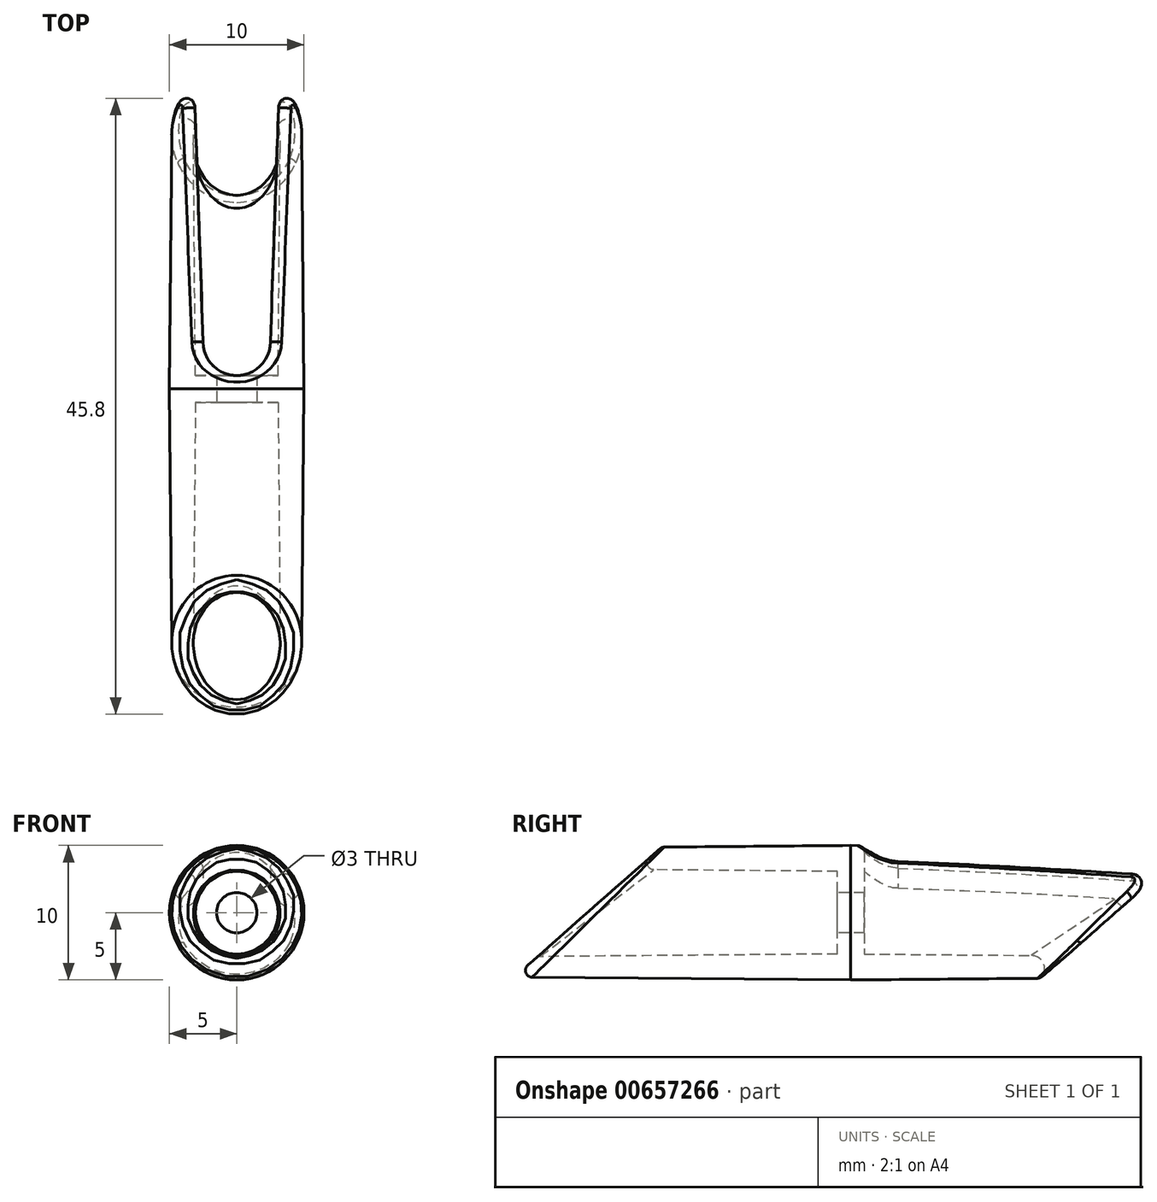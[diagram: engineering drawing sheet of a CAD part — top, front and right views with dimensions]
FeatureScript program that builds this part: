
annotation { "Feature Type Name" : "Feature", "Feature Type Description" : "" }
export const myFeature = defineFeature(function(context is Context, id is Id, definition is map)
    precondition{}
    {
        {
            var Q0;
            Q0=qCreatedBy(makeId("Right.planeOp"),FACE);
            var sketch = newSketch(context, id + "F0", { "sketchPlane" : qUnion([Q0])});
            skLineSegment(sketch, "E0", {"start": v(0, 0) * mm, "end": v(360.3, 0) * mm, "construction": true});
            skLineSegment(sketch, "E1", {"start": v(0, 0) * mm, "end": v(0, 1.5) * mm, "construction": true});
            skLineSegment(sketch, "E2", {"start": v(0, 1.5) * mm, "end": v(1, 1.5) * mm});
            skLineSegment(sketch, "E3", {"start": v(1, 1.5) * mm, "end": v(1, 3.07) * mm});
            skLineSegment(sketch, "E4", {"start": v(1, 3.07) * mm, "end": v(303.63, 3.07) * mm, "construction": true});
            skLineSegment(sketch, "E5", {"start": v(1, 3.07) * mm, "end": v(25, 3.28) * mm});
            skLineSegment(sketch, "E6", {"start": v(0, 5) * mm, "end": v(0, 106.1) * mm, "construction": true});
            skLineSegment(sketch, "E7", {"start": v(0, 5) * mm, "end": v(82.2, 5) * mm, "construction": true});
            skLineSegment(sketch, "E8", {"start": v(0, 5) * mm, "end": v(25, 4.78) * mm});
            skLineSegment(sketch, "E9", {"start": v(25, 3.28) * mm, "end": v(25, 4.78) * mm});
            skLineSegment(sketch, "E10.MirrorCS", {"start": v(0, 1.5) * mm, "end": v(-1, 1.5) * mm});
            skLineSegment(sketch, "E11.MirrorCS", {"start": v(-1, 1.5) * mm, "end": v(-1, 3.07) * mm});
            skLineSegment(sketch, "E12.MirrorCS", {"start": v(-1, 3.07) * mm, "end": v(-25, 3.28) * mm});
            skLineSegment(sketch, "E13.MirrorCS", {"start": v(-25, 3.28) * mm, "end": v(-25, 4.78) * mm});
            skLineSegment(sketch, "E14.MirrorCS", {"start": v(0, 5) * mm, "end": v(-25, 4.78) * mm});
            skSolve(sketch);
        }
        {
            var Q0;
            Q0=makeQuery(id+"F0.imprint","IMPRINT",FACE,{"disambiguationData":[TD([[makeQuery(id+"F0.imprint","IMPRINT",EDGE,{"derivedFrom":sQuery(id+"F0.wireOp",EDGE,"E2")}),1.0]])]});
            var Q1;
            Q1=sQuery(id+"F0.wireOp",EDGE,"E0");
            revolve(context, id + "F1", {"surfaceOperationType" : NewSurfaceOperationType.NEW, "entities" : qUnion([Q0]), "axis" : qUnion([Q1]), "revolveType" : RevolveType.FULL});
        }
        {
            var Q0;
            Q0=qCreatedBy(makeId("Top.planeOp"),FACE);
            var sketch = newSketch(context, id + "F2", { "sketchPlane" : qUnion([Q0])});
            skLineSegment(sketch, "E15", {"start": v(1.5, 1) * mm, "end": v(3.07, 1) * mm, "construction": true});
            skLineSegment(sketch, "E16", {"start": v(-3.07, 1) * mm, "end": v(-1.5, 1) * mm, "construction": true});
            skLineSegment(sketch, "E17", {"start": v(1.5, 1) * mm, "end": v(-1.5, 1) * mm, "construction": true});
            skLineSegment(sketch, "E18", {"start": v(0, 1) * mm, "end": v(0, 704.1) * mm, "construction": true});
            skArc(sketch, "E19", {"start": v(-2.5, 3.5) * mm, "mid": v(0, 1) * mm, "end": v(2.5, 3.5) * mm});
            skLineSegment(sketch, "E20", {"start": v(0, 3.5) * mm, "end": v(2.5, 3.5) * mm, "construction": true});
            skLineSegment(sketch, "E21", {"start": v(2.5, 3.5) * mm, "end": v(3.25, 25) * mm});
            skLineSegment(sketch, "E22.MirrorCS", {"start": v(-2.5, 3.5) * mm, "end": v(-3.25, 25) * mm});
            skLineSegment(sketch, "E23.0", {"start": v(4.78, 25) * mm, "end": v(3.25, 25) * mm});
            skLineSegment(sketch, "E24.trimOffspring", {"start": v(-3.25, 25) * mm, "end": v(-4.78, 25) * mm});
            skPoint(sketch, "E25.orphan", {"position": v(-3.32, 27.03) * mm});
            skPoint(sketch, "E26.start.orphan", {"position": v(3.32, 27.03) * mm});
            skPoint(sketch, "E27.visualSharp", {"position": v(3.25, 25) * mm});
            skLineSegment(sketch, "E27.filletArc", {"start": v(3.25, 25) * mm, "end": v(3.25, 25) * mm});
            skPoint(sketch, "E28.visualSharp", {"position": v(-3.25, 25) * mm});
            skLineSegment(sketch, "E28.filletArc", {"start": v(-3.25, 25) * mm, "end": v(-3.25, 25) * mm});
            skLineSegment(sketch, "E29", {"start": v(4.78, 25) * mm, "end": v(4.78, 27.96) * mm});
            skLineSegment(sketch, "E30", {"start": v(4.78, 27.96) * mm, "end": v(-5, 27.96) * mm});
            skLineSegment(sketch, "E31", {"start": v(-5, 27.96) * mm, "end": v(-4.78, 25) * mm});
            skSolve(sketch);
        }
        {
            var Q0;
            Q0 = qSketchRegion(id + "F2", true);
            extrude(context, id + "F3", {"entities" : qUnion([Q0]), "operationType" : NewBodyOperationType.REMOVE, "depth" : 25 * mm, "offsetDistance" : 25 * mm});
        }
        {
            var Q0;
            Q0=qCreatedBy(makeId("Right.planeOp"),FACE);
            var sketch = newSketch(context, id + "F4", { "sketchPlane" : qUnion([Q0])});
            skLineSegment(sketch, "E32", {"start": v(-25, 4.78) * mm, "end": v(0, 5) * mm, "construction": true});
            skLineSegment(sketch, "E33", {"start": v(0, -5) * mm, "end": v(-25, -4.78) * mm, "construction": true});
            skLineSegment(sketch, "E34", {"start": v(27.27, 6.7) * mm, "end": v(9.74, -8.75) * mm});
            skLineSegment(sketch, "E35", {"start": v(-25, -4.78) * mm, "end": v(-3.2, 14.45) * mm});
            skLineSegment(sketch, "E36", {"start": v(-25, -4.78) * mm, "end": v(-29.64, -4.74) * mm});
            skLineSegment(sketch, "E37", {"start": v(-29.64, -4.74) * mm, "end": v(-29.64, 15.92) * mm});
            skLineSegment(sketch, "E38", {"start": v(-29.64, 15.92) * mm, "end": v(-3.2, 14.45) * mm});
            skLineSegment(sketch, "E39", {"start": v(9.74, -8.75) * mm, "end": v(32.4, -8.95) * mm});
            skLineSegment(sketch, "E40", {"start": v(32.4, -8.95) * mm, "end": v(32.4, 6.67) * mm});
            skLineSegment(sketch, "E41", {"start": v(32.4, 6.67) * mm, "end": v(27.27, 6.7) * mm});
            skSolve(sketch);
        }
        {
            var Q0;
            Q0 = qSketchRegion(id + "F4", true);
            extrude(context, id + "F5", {"entities" : qUnion([Q0]), "operationType" : NewBodyOperationType.REMOVE, "oppositeDirection" : true, "depth" : 25 * mm, "offsetDistance" : 25 * mm, "symmetric" : true});
        }
        {
            var Q0;
            Q0=makeQuery(id+"F5.boolean.opBoolean","INTERSECT",EDGE,{"derivedFrom":[makeQuery(id+"F3.boolean.opBoolean","COPY",FACE,{"derivedFrom":makeQuery(id+"F3.opExtrude","SWEPT_FACE",FACE,{"disambiguationData":[OSD([sQuery(id+"F2.wireOp",EDGE,"E22.MirrorCS")])]})}),makeQuery(id+"F5.opExtrude","SWEPT_FACE",FACE,{"disambiguationData":[OSD([sQuery(id+"F4.wireOp",EDGE,"E34")])]})]});
            var Q1;
            Q1=makeQuery(id+"F5.boolean.opBoolean","INTERSECT",EDGE,{"derivedFrom":[makeQuery(id+"F1.opRevolve","SWEPT_FACE",FACE,{"disambiguationData":[OSD([sQuery(id+"F0.wireOp",EDGE,"E5")])]}),makeQuery(id+"F5.opExtrude","SWEPT_FACE",FACE,{"disambiguationData":[OSD([sQuery(id+"F4.wireOp",EDGE,"E34")])]})]});
            var Q2;
            Q2=makeQuery(id+"F5.boolean.opBoolean","INTERSECT",EDGE,{"derivedFrom":[makeQuery(id+"F3.boolean.opBoolean","COPY",FACE,{"derivedFrom":makeQuery(id+"F3.opExtrude","SWEPT_FACE",FACE,{"disambiguationData":[OSD([sQuery(id+"F2.wireOp",EDGE,"E21")])]})}),makeQuery(id+"F5.opExtrude","SWEPT_FACE",FACE,{"disambiguationData":[OSD([sQuery(id+"F4.wireOp",EDGE,"E34")])]})]});
            fillet(context, id + "F6", {"entities" : qUnion([Q0, Q1, Q2]), "radius" : 1 * mm, "tangentPropagation" : true, "allowEdgeOverflow" : false});
        }
        {
            var Q0;
            Q0=makeQuery(id+"F5.boolean.opBoolean","INTERSECT",EDGE,{"derivedFrom":[makeQuery(id+"F1.opRevolve","SWEPT_FACE",FACE,{"disambiguationData":[OSD([sQuery(id+"F0.wireOp",EDGE,"E8")])]}),makeQuery(id+"F5.opExtrude","SWEPT_FACE",FACE,{"disambiguationData":[OSD([sQuery(id+"F4.wireOp",EDGE,"E34")])]})]});
            var Q1;
            Q1=makeQuery(id+"F6.opFillet","BLEND_EDGE",EDGE,{"blendedFrom":[makeQuery(id+"F5.boolean.opBoolean","INTERSECT",EDGE,{"derivedFrom":[makeQuery(id+"F3.boolean.opBoolean","COPY",FACE,{"derivedFrom":makeQuery(id+"F3.opExtrude","SWEPT_FACE",FACE,{"disambiguationData":[OSD([sQuery(id+"F2.wireOp",EDGE,"E22.MirrorCS")])]})}),makeQuery(id+"F5.opExtrude","SWEPT_FACE",FACE,{"disambiguationData":[OSD([sQuery(id+"F4.wireOp",EDGE,"E34")])]})]}),makeQuery(id+"F1.opRevolve","SWEPT_FACE",FACE,{"disambiguationData":[OSD([sQuery(id+"F0.wireOp",EDGE,"E8")])]})],"blendedInto":[makeQuery(id+"F1.opRevolve","SWEPT_FACE",FACE,{"disambiguationData":[OSD([sQuery(id+"F0.wireOp",EDGE,"E8")])]})]});
            var Q2;
            Q2=makeQuery(id+"F3.boolean.opBoolean","INTERSECT",EDGE,{"derivedFrom":[makeQuery(id+"F1.opRevolve","SWEPT_FACE",FACE,{"disambiguationData":[OSD([sQuery(id+"F0.wireOp",EDGE,"E8")])]}),makeQuery(id+"F3.opExtrude","SWEPT_FACE",FACE,{"disambiguationData":[OSD([sQuery(id+"F2.wireOp",EDGE,"E22.MirrorCS")])]})]});
            var Q3;
            Q3=makeQuery(id+"F3.boolean.opBoolean","INTERSECT",EDGE,{"derivedFrom":[makeQuery(id+"F1.opRevolve","SWEPT_FACE",FACE,{"disambiguationData":[OSD([sQuery(id+"F0.wireOp",EDGE,"E8")])]}),makeQuery(id+"F3.opExtrude","SWEPT_FACE",FACE,{"disambiguationData":[OSD([sQuery(id+"F2.wireOp",EDGE,"E19")])]})]});
            var Q4;
            Q4=makeQuery(id+"F6.opFillet","BLEND_EDGE",EDGE,{"blendedFrom":[makeQuery(id+"F5.boolean.opBoolean","INTERSECT",EDGE,{"derivedFrom":[makeQuery(id+"F3.boolean.opBoolean","COPY",FACE,{"derivedFrom":makeQuery(id+"F3.opExtrude","SWEPT_FACE",FACE,{"disambiguationData":[OSD([sQuery(id+"F2.wireOp",EDGE,"E21")])]})}),makeQuery(id+"F5.opExtrude","SWEPT_FACE",FACE,{"disambiguationData":[OSD([sQuery(id+"F4.wireOp",EDGE,"E34")])]})]}),makeQuery(id+"F1.opRevolve","SWEPT_FACE",FACE,{"disambiguationData":[OSD([sQuery(id+"F0.wireOp",EDGE,"E8")])]})],"blendedInto":[makeQuery(id+"F1.opRevolve","SWEPT_FACE",FACE,{"disambiguationData":[OSD([sQuery(id+"F0.wireOp",EDGE,"E8")])]})]});
            var Q5;
            Q5=makeQuery(id+"F5.boolean.opBoolean","INTERSECT",EDGE,{"derivedFrom":[makeQuery(id+"F1.opRevolve","SWEPT_FACE",FACE,{"disambiguationData":[OSD([sQuery(id+"F0.wireOp",EDGE,"E14.MirrorCS")])]}),makeQuery(id+"F5.opExtrude","SWEPT_FACE",FACE,{"disambiguationData":[OSD([sQuery(id+"F4.wireOp",EDGE,"E35")])]})]});
            var Q6;
            Q6=makeQuery(id+"F5.boolean.opBoolean","INTERSECT",EDGE,{"derivedFrom":[makeQuery(id+"F1.opRevolve","SWEPT_FACE",FACE,{"disambiguationData":[OSD([sQuery(id+"F0.wireOp",EDGE,"E12.MirrorCS")])]}),makeQuery(id+"F5.opExtrude","SWEPT_FACE",FACE,{"disambiguationData":[OSD([sQuery(id+"F4.wireOp",EDGE,"E35")])]})]});
            fillet(context, id + "F7", {"entities" : qUnion([Q0, Q1, Q2, Q3, Q4, Q5, Q6]), "radius" : 0.5 * mm, "tangentPropagation" : true, "allowEdgeOverflow" : false});
        }
    });
